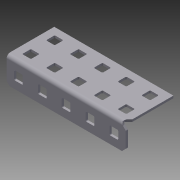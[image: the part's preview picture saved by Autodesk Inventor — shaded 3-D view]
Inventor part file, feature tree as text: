
AUTODESK INVENTOR PART (.ipt)
format: ipt  version: 2012 (Build 160160000, 160)  size: 898,560 bytes
history: native  units: in
note: dims shown in document units (in); Inventor stores cm internally (conversion verified against a paired STEP export)
features: plane x2, split x2, other x1, imported_body x1
ambient origin geometry x8: Origin, YZ Plane, XZ Plane, XY Plane, X Axis, Y Axis, Z Axis, Center Point
feature tree (6):
  parser-record x1  (decoder bookkeeping rows leaked as tree rows — omitted from the tree; the rows remain in map.json)
  imported_body  "Base1"
  plane  "Work Plane1"
  split  "Split1"
  plane  "Work Plane2"
  split  "Split2"
